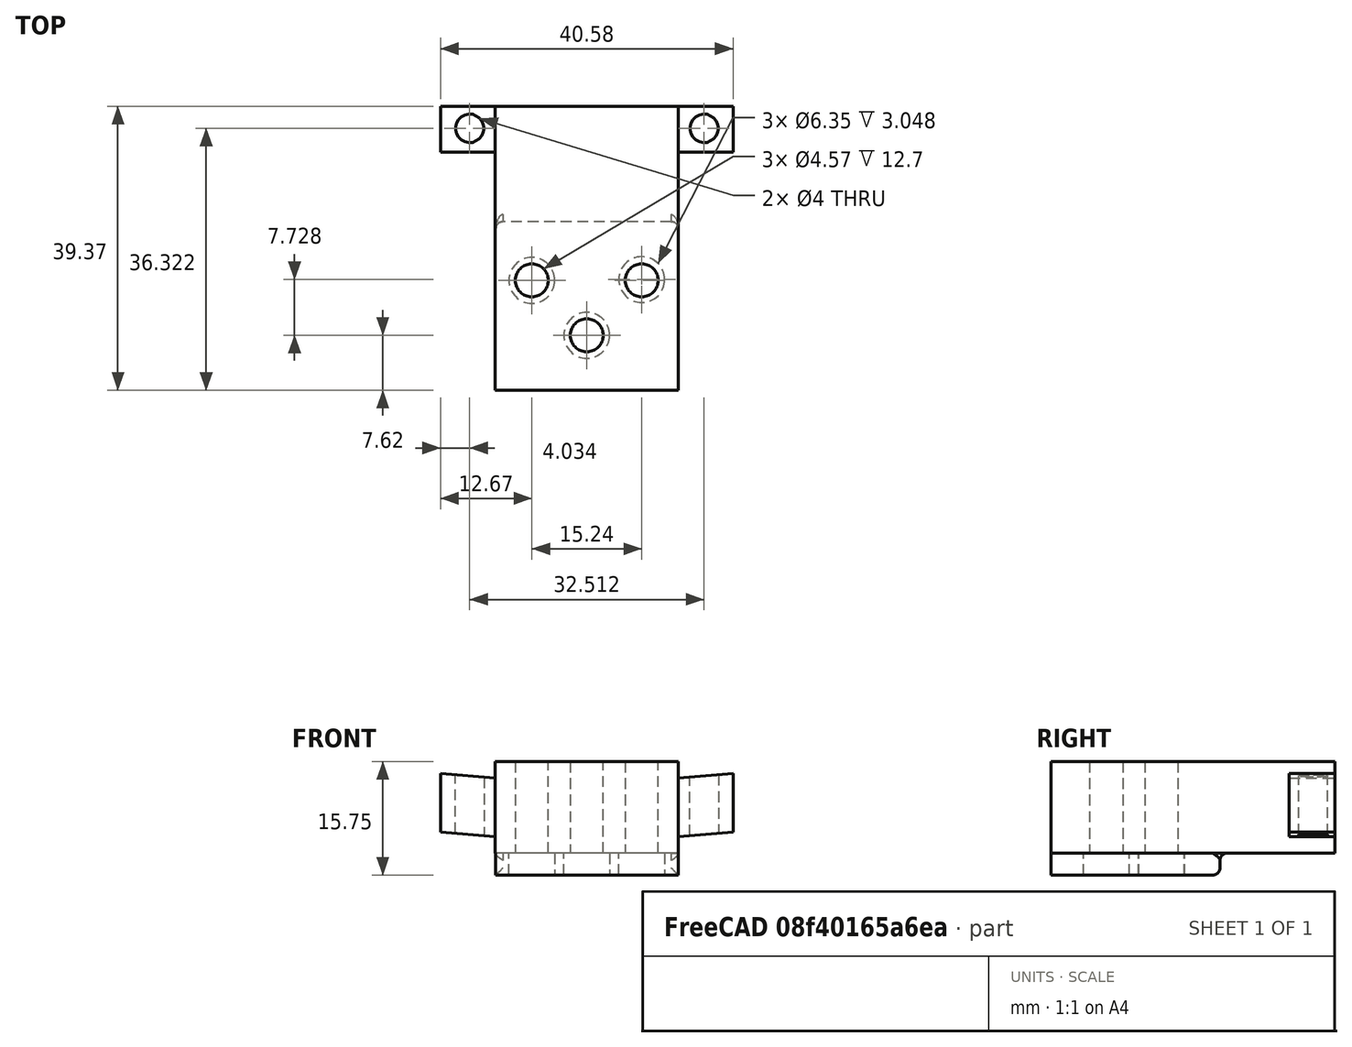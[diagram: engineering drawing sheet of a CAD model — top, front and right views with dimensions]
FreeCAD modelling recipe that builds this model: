
FCSTD DOCUMENT  (FreeCAD 0.18.1R)
Label: crossbow_bow_rev_03
License: All rights reserved
LicenseURL: http://en.wikipedia.org/wiki/All_rights_reserved
objects: Sketcher::SketchObject×6, PartDesign::Pad×3, PartDesign::Pocket×3, PartDesign::Fillet×1, PartDesign::Body×1, Mesh::Feature×1
note: 20 computed .brp shape members not serialized (recipe doc carries the construction recipe); baked Part::Feature solids carry a one-line shape summary decoded from their .brp

FEATURE [Sketcher::SketchObject] Sketch
  MapMode = 5
  Support = -> [XY_Plane]
  sketch-geometry (5):
    g0: LineSegment StartX=0 StartY=0 StartZ=0 EndX=12.7 EndY=0 EndZ=0
    g1: LineSegment StartX=0 StartY=0 StartZ=0 EndX=-12.7 EndY=0 EndZ=0
    g2: LineSegment StartX=-12.7 StartY=0 StartZ=0 EndX=-12.7 EndY=33.02 EndZ=0
    g3: LineSegment StartX=12.7 StartY=0 StartZ=0 EndX=12.7 EndY=33.02 EndZ=0
    g4: LineSegment StartX=12.7 StartY=33.02 StartZ=0 EndX=-12.7 EndY=33.02 EndZ=0
  constraints (14):
    c: Coincident(g0,g-1)
    c: PointOnObject(g0,g-1)
    c: Coincident(g1,g0)
    c: PointOnObject(g1,g-1)
    c: Coincident(g2,g1)
    c: Vertical(g2)
    c: Coincident(g3,g0)
    c: Vertical(g3)
    c: Coincident(g4,g3)
    c: Coincident(g4,g2)
    c: Horizontal(g4)
    c: DistanceX(g4,g4) = 25.4
    c: DistanceX(g0,g0) = 12.7
    c: DistanceY(g2,g2) = 33.02
FEATURE [PartDesign::Pad] Pad
  Length = 12.7
  Length2 = 100.076
  Profile = -> Sketch
  Type = 0
FEATURE [Sketcher::SketchObject] Sketch001
  MapMode = 5
  Placement = pos=(0,33.02,0) rot=(0,0.707107,0.707107;3.14159rad)
  Support = -> [Pad]
  sketch-geometry (17):
    g0: LineSegment StartX=-20.2935 StartY=2.921 StartZ=0 EndX=-12.7 EndY=2.286 EndZ=0
    g1: LineSegment StartX=-12.7 StartY=2.286 StartZ=0 EndX=-8.55 EndY=2.286 EndZ=0
    g2: LineSegment StartX=-20.2935 StartY=2.921 StartZ=0 EndX=-20.32 EndY=5.46086 EndZ=0
    g3: LineSegment StartX=-20.32 StartY=8.50914 StartZ=0 EndX=-20.2935 EndY=11.049 EndZ=0
    g4: LineSegment StartX=-20.2935 StartY=11.049 StartZ=0 EndX=-12.7 EndY=10.414 EndZ=0
    g5: LineSegment StartX=-12.7 StartY=2.286 StartZ=0 EndX=-12.7 EndY=0 EndZ=0
    g6: LineSegment StartX=-12.7 StartY=0 StartZ=0 EndX=12.7 EndY=0 EndZ=0
    g7: LineSegment StartX=12.7 StartY=0 StartZ=0 EndX=12.7 EndY=2.286 EndZ=0
    g8: LineSegment StartX=12.7 StartY=2.286 StartZ=0 EndX=20.2935 EndY=2.92097 EndZ=0
    g9: LineSegment StartX=20.2935 StartY=2.92097 StartZ=0 EndX=20.32 EndY=5.46084 EndZ=0
    g10: LineSegment StartX=20.2934 StartY=8.50897 StartZ=0 EndX=20.2935 EndY=11.049 EndZ=0
    g11: LineSegment StartX=20.2935 StartY=11.049 StartZ=0 EndX=12.7 EndY=10.414 EndZ=0
    g12: LineSegment StartX=12.7 StartY=10.414 StartZ=0 EndX=12.7 EndY=12.7 EndZ=0
    g13: LineSegment StartX=-12.7 StartY=10.414 StartZ=0 EndX=-12.7 EndY=12.7 EndZ=0
    g14: LineSegment StartX=-12.7 StartY=12.7 StartZ=0 EndX=12.7 EndY=12.7 EndZ=0
    g15: LineSegment StartX=-20.32 StartY=5.46086 StartZ=0 EndX=-20.32 EndY=8.50886 EndZ=0
    g16: LineSegment StartX=20.32 StartY=5.46084 StartZ=0 EndX=20.32 EndY=8.50884 EndZ=0
  constraints (53):
    c: Angle(g-1,g0) = 3.05816
    c: Distance(g0,g-2) = 12.7
    c: Distance(g0,g-1) = 2.286
    c: Distance(g0) = 7.62
    c: Coincident(g1,g0)
    c: Horizontal(g1)
    c: Coincident(g2,g0)
    c: Distance(g2) = 2.54
    c: Coincident(g4,g3)
    c: Distance(g4) = 7.62
    c: Distance(g3) = 2.54
    c: Distance(g4,g-2) = 12.7
    c: Coincident(g5,g0)
    c: PointOnObject(g5,g-1)
    c: Vertical(g5)
    c: Coincident(g6,g5)
    c: PointOnObject(g6,g-1)
    c: Coincident(g7,g6)
    c: Vertical(g7)
    c: Coincident(g8,g7)
    c: Coincident(g9,g8)
    c: Coincident(g11,g10)
    c: Coincident(g12,g11)
    c: Vertical(g12)
    c: Coincident(g13,g4)
    c: Vertical(g13)
    c: Coincident(g14,g13)
    c: Coincident(g14,g12)
    c: Horizontal(g14)
    c: Distance(g8) = 7.62
    c: Distance(g9) = 2.54
    c: Distance(g10) = 2.54
    c: Distance(g11) = 7.62
    c: DistanceY(g7,g7) = 2.286
    c: DistanceY(g12,g12) = 2.286
    c: DistanceY(g13,g13) = 2.286
    c: Angle(g8,g-1) = 3.05817
    c: DistanceX(g14,g14) = 25.4
    c: DistanceX(g6,g6) = 25.4
    c: Distance(g12,g-1) = 12.7
    c: Coincident(g15,g2)
    c: Vertical(g15)
    c: Coincident(g16,g9)
    c: Vertical(g16)
    c: Distance(g16) = 3.048
    c: Distance(g15) = 3.048
    c: Distance(g3,g16) = 40.64
    c: Distance(g9,g2) = 40.64
    c: Distance(g0,g3) = 8.128
    c: Distance(g10,g8) = 8.128
    c: Distance(g3,g-2) = 20.32
    c: Distance(g9,g-2) = 20.32
    c: Distance(g2,g-2) = 20.32
FEATURE [PartDesign::Pad] Pad001
  BaseFeature = -> Pad
  Length = 6.35
  Length2 = 100.076
  Profile = -> Sketch001
  Type = 0
FEATURE [Sketcher::SketchObject] Sketch002
  MapMode = 5
  Placement = pos=(0,0,0) rot=(1,0,0;3.14159rad)
  Support = -> [Pad001]
  sketch-geometry (3):
    g0: Circle CenterX=0 CenterY=-7.62 CenterZ=0 NormalX=0 NormalY=0 NormalZ=1 AngleXU=0 Radius=2.286
    g1: Circle CenterX=7.62 CenterY=-15.24 CenterZ=0 NormalX=0 NormalY=0 NormalZ=1 AngleXU=0 Radius=2.286
    g2: Circle CenterX=-7.62 CenterY=-15.24 CenterZ=0 NormalX=0 NormalY=0 NormalZ=1 AngleXU=0 Radius=2.286
  constraints (9):
    c: PointOnObject(g0,g-2)
    c: Distance(g0,g-1) = 7.62
    c: Distance(g1,g-1) = 15.24
    c: Distance(g1,g-2) = 7.62
    c: Distance(g2,g-1) = 15.24
    c: Distance(g2,g-2) = 7.62
    c: Radius(g0) = 2.286
    c: Radius(g1) = 2.286
    c: Radius(g2) = 2.286
FEATURE [PartDesign::Pocket] Pocket
  BaseFeature = -> Pad001
  Length = 30.48
  Length2 = 100.076
  Profile = -> Sketch002
  Type = 0
FEATURE [Sketcher::SketchObject] Sketch003
  MapMode = 5
  Placement = pos=(20.2935,0,-6.98444e-09) rot=(0.57735,0.57735,0.57735;2.0944rad)
  Support = -> [Pocket]
  sketch-geometry (2):
    g0: Circle CenterX=16.256 CenterY=-36.195 CenterZ=0 NormalX=0 NormalY=0 NormalZ=1 AngleXU=0 Radius=1.905
    g1: Circle CenterX=-16.256 CenterY=-36.195 CenterZ=0 NormalX=0 NormalY=0 NormalZ=1 AngleXU=0 Radius=1.905
  constraints (6):
    c: Distance(g0,g-2) = 16.256
    c: Distance(g0,g-1) = 36.195
    c: Distance(g1,g-2) = 16.256
    c: Distance(g1,g-1) = 36.195
    c: Radius(g0) = 1.905
    c: Radius(g1) = 1.905
FEATURE [PartDesign::Pocket] Pocket001
  BaseFeature = -> Pocket
  Length = 30.48
  Length2 = 100.076
  Profile = -> Sketch003
  Type = 0
FEATURE [Sketcher::SketchObject] Sketch004
  MapMode = 5
  Placement = pos=(0,0,12.7) rot=(0,0,1;0rad)
  Support = -> [Pocket001]
  sketch-geometry (2):
    g0: Circle CenterX=16.256 CenterY=36.322 CenterZ=0 NormalX=0 NormalY=0 NormalZ=1 AngleXU=0 Radius=2
    g1: Circle CenterX=-16.256 CenterY=36.322 CenterZ=0 NormalX=0 NormalY=0 NormalZ=1 AngleXU=0 Radius=2
  constraints (6):
    c: Distance(g1,g-2) = 16.256
    c: Radius(g1) = 2
    c: Radius(g0) = 2
    c: Distance(g0,g-2) = 16.256
    c: Distance(g0,g-1) = 36.322
    c: Distance(g1,g-1) = 36.322
FEATURE [PartDesign::Pocket] Pocket002
  BaseFeature = -> Pocket001
  Length = 30.48
  Length2 = 100.076
  Profile = -> Sketch004
  Type = 0
FEATURE [Sketcher::SketchObject] Sketch005
  MapMode = 5
  Placement = pos=(0,0,0) rot=(1,0,0;3.14159rad)
  Support = -> [Pocket002]
  sketch-geometry (7):
    g0: LineSegment StartX=-12.6159 StartY=0 StartZ=0 EndX=12.6916 EndY=0 EndZ=0
    g1: LineSegment StartX=12.6916 StartY=0 StartZ=0 EndX=12.6916 EndY=-23.3934 EndZ=0
    g2: LineSegment StartX=12.6916 StartY=-23.3934 StartZ=0 EndX=-12.6159 EndY=-23.3934 EndZ=0
    g3: LineSegment StartX=-12.6159 StartY=-23.3934 StartZ=0 EndX=-12.6159 EndY=0 EndZ=0
    g4: Circle CenterX=0 CenterY=-7.62 CenterZ=0 NormalX=0 NormalY=0 NormalZ=1 AngleXU=0 Radius=3.175
    g5: Circle CenterX=7.61962 CenterY=-15.3479 CenterZ=0 NormalX=0 NormalY=0 NormalZ=1 AngleXU=0 Radius=3.175
    g6: Circle CenterX=-7.62 CenterY=-15.24 CenterZ=0 NormalX=0 NormalY=0 NormalZ=1 AngleXU=0 Radius=3.175
  constraints (17):
    c: Coincident(g0,g1)
    c: Coincident(g1,g2)
    c: Coincident(g2,g3)
    c: Coincident(g3,g0)
    c: Horizontal(g0)
    c: Horizontal(g2)
    c: Vertical(g1)
    c: Vertical(g3)
    c: PointOnObject(g0,g-1)
    c: PointOnObject(g4,g-2)
    c: Distance(g4,g-1) = 7.62
    c: Distance(g6,g5) = 15.24
    c: Distance(g6,g0) = 15.24
    c: Distance(g6,g-2) = 7.62
    c: Radius(g4) = 3.175
    c: Radius(g5) = 3.175
    c: Radius(g6) = 3.175
FEATURE [PartDesign::Pad] Pad002
  BaseFeature = -> Pocket002
  Length = 3.048
  Length2 = 100.076
  Profile = -> Sketch005
  Type = 0
FEATURE [PartDesign::Fillet] Fillet
  Base = -> Pad002 [Face14]
  BaseFeature = -> Pad002
  Radius = 0.999998
FEATURE [PartDesign::Body] Body
  Group = -> [Sketch,Pad,Sketch001,Pad001,Sketch002,Pocket,Sketch003,Pocket001,Sketch004,Pocket002,Sketch005,Pad002,Fillet]
  Origin = -> Origin
  Tip = -> Fillet
FEATURE [Mesh::Feature] Mesh  label="Fillet (Meshed)"
